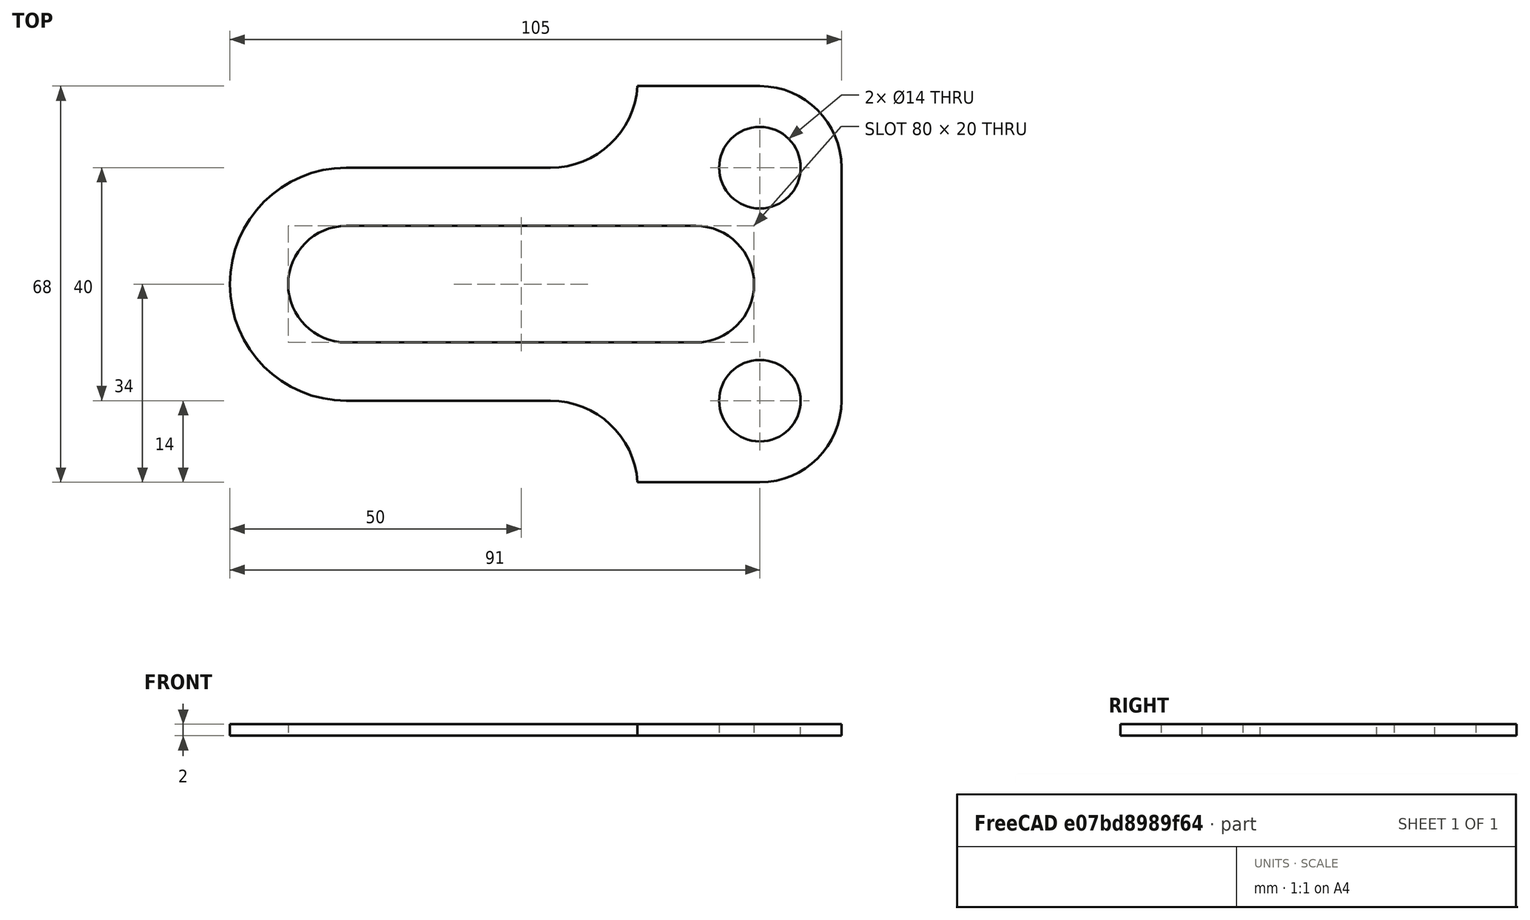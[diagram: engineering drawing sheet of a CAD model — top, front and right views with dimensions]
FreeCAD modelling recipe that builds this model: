
FCSTD DOCUMENT  (FreeCAD 0.16R6700 (Git))
Label: ejer3 final
License: All rights reserved
LicenseURL: http://en.wikipedia.org/wiki/All_rights_reserved
objects: Sketcher::SketchObject×1, PartDesign::Pad×1
note: 3 computed .brp shape members not serialized (recipe doc carries the construction recipe); baked Part::Feature solids carry a one-line shape summary decoded from their .brp

FEATURE [Sketcher::SketchObject] Sketch
  sketch-geometry (16):
    g0: ArcOfCircle CenterX=-60 CenterY=0 CenterZ=0 NormalX=0 NormalY=0 NormalZ=1 Radius=10 StartAngle=1.5708 EndAngle=4.71239
    g1: ArcOfCircle CenterX=0 CenterY=0 CenterZ=0 NormalX=0 NormalY=0 NormalZ=1 Radius=10 StartAngle=4.71239 EndAngle=7.85398
    g2: Circle CenterX=11 CenterY=20 CenterZ=0 NormalX=0 NormalY=0 NormalZ=1 Radius=7
    g3: Circle CenterX=11 CenterY=-20 CenterZ=0 NormalX=0 NormalY=0 NormalZ=1 Radius=7
    g4: LineSegment StartX=-10 StartY=34 StartZ=0 EndX=11 EndY=34 EndZ=0
    g5: LineSegment StartX=25 StartY=20 StartZ=0 EndX=25 EndY=-20 EndZ=0
    g6: LineSegment StartX=11 StartY=-34 StartZ=0 EndX=-10 EndY=-34 EndZ=0
    g7: LineSegment StartX=-24.9666 StartY=-20 StartZ=0 EndX=-60 EndY=-20 EndZ=0
    g8: LineSegment StartX=-60 StartY=20 StartZ=0 EndX=-24.9666 EndY=20 EndZ=0
    g9: ArcOfCircle CenterX=-60 CenterY=0 CenterZ=0 NormalX=0 NormalY=0 NormalZ=1 Radius=20 StartAngle=1.5708 EndAngle=4.71239
    g10: LineSegment StartX=-60 StartY=-10 StartZ=0 EndX=2.144e-09 EndY=-10 EndZ=0
    g11: LineSegment StartX=-60 StartY=10 StartZ=0 EndX=-2.082e-09 EndY=10 EndZ=0
    g12: ArcOfCircle CenterX=-24.9666 CenterY=35 CenterZ=0 NormalX=0 NormalY=0 NormalZ=1 Radius=15 StartAngle=4.71239 EndAngle=6.21647
    g13: ArcOfCircle CenterX=-24.9666 CenterY=-35 CenterZ=0 NormalX=0 NormalY=0 NormalZ=1 Radius=15 StartAngle=0.0667161 EndAngle=1.5708
    g14: ArcOfCircle CenterX=11 CenterY=20 CenterZ=0 NormalX=0 NormalY=0 NormalZ=1 Radius=14 StartAngle=0 EndAngle=1.5708
    g15: ArcOfCircle CenterX=11 CenterY=-20 CenterZ=0 NormalX=0 NormalY=0 NormalZ=1 Radius=14 StartAngle=4.71239 EndAngle=6.28319
  constraints (48):
    c: PointOnObject(g0,g-1)
    c: Coincident(g1,g-1)
    c: Radius(g0) = 10
    c: Radius(g1) = 10
    c: Radius(g2) = 7
    c: Radius(g3) = 7
    c: DistanceX(g0,g-1) = 60
    c: Horizontal(g4)
    c: Vertical(g5)
    c: Horizontal(g6)
    c: Horizontal(g8)
    c: Horizontal(g7)
    c: Coincident(g9,g0)
    c: Coincident(g9,g8)
    c: Coincident(g9,g7)
    c: Tangent(g7,g9)
    c: Tangent(g9,g8)
    c: Horizontal(g10)
    c: Horizontal(g11)
    c: Tangent(g8,g12) = -1.5708
    c: Tangent(g7,g13) = -1.5708
    c: Tangent(g4,g14) = 1.5708
    c: Tangent(g5,g14) = 1.5708
    c: Tangent(g5,g15) = 1.5708
    c: Tangent(g6,g15) = 1.5708
    c: DistanceY(g6,g4) = 68
    c: DistanceX(g6,g5) = 35
    c: DistanceX(g4,g5) = 35
    c: Radius(g13) = 15
    c: Coincident(g6,g13)
    c: Radius(g12) = 15
    c: Coincident(g12,g4)
    c: Radius(g9) = 20
    c: Symmetric(g4,g6,g-1)
    c: DistanceY(g3,g2) = 40
    c: Symmetric(g3,g2,g-1)
    c: Radius(g15) = 14
    c: Equal(g15,g14)
    c: Coincident(g0,g11)
    c: Coincident(g0,g10)
    c: Coincident(g1,g10)
    c: Coincident(g1,g11)
    c: Tangent(g1,g11)
    c: Tangent(g1,g10)
    c: Tangent(g11,g0)
    c: Tangent(g0,g10)
    c: DistanceX(g0,g6) = 50
    c: DistanceX(g2,g5) = 14
FEATURE [PartDesign::Pad] Pad
  Length = 2
  Length2 = 100
  Sketch = -> Sketch
  Type = 0
